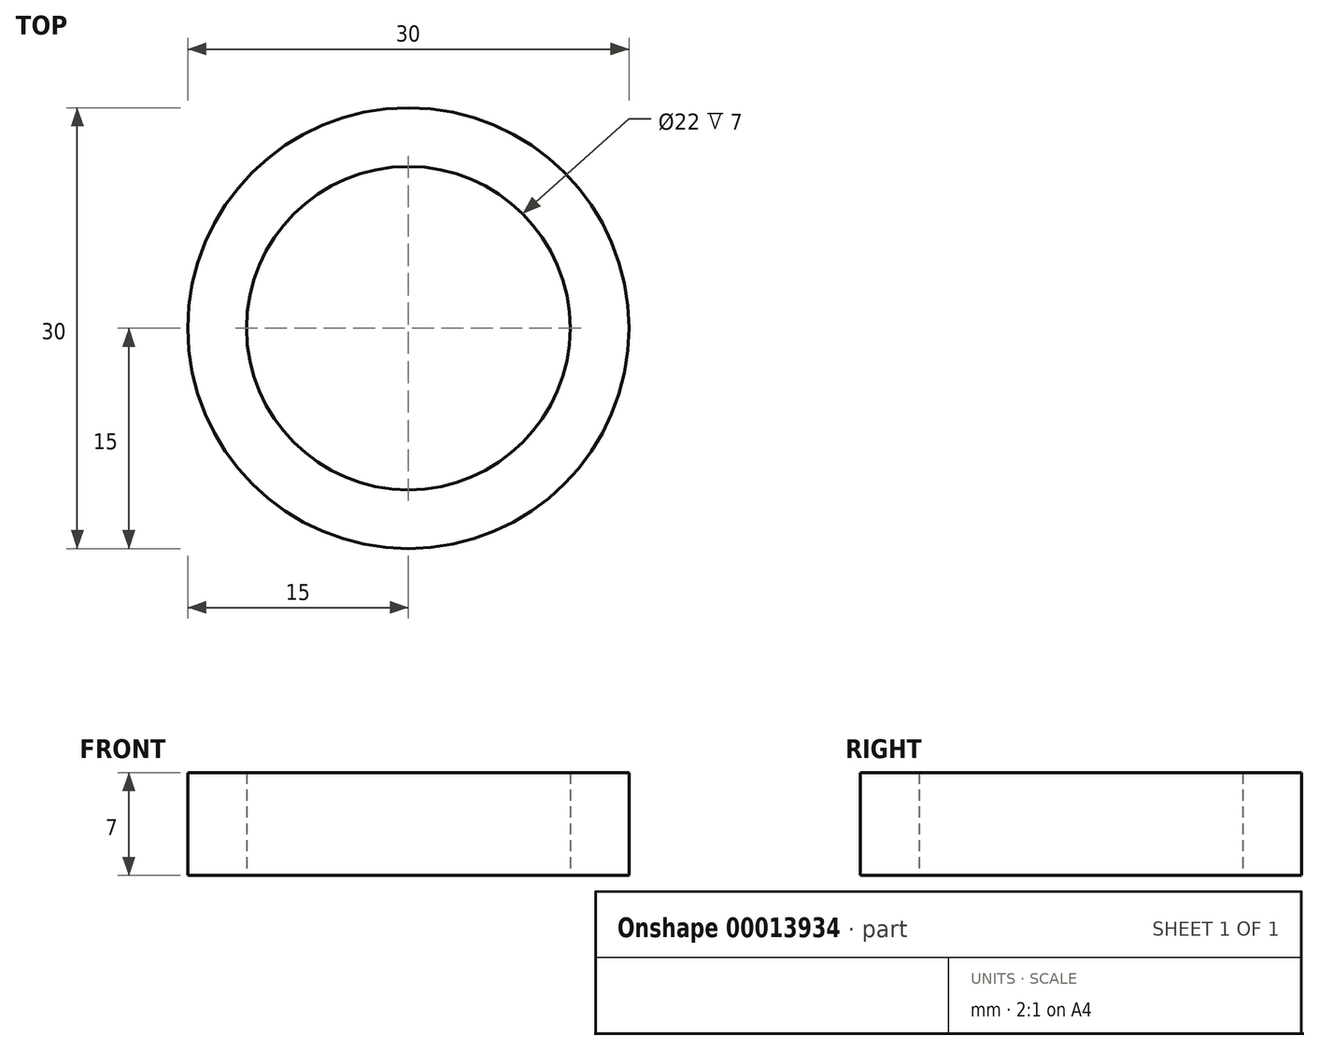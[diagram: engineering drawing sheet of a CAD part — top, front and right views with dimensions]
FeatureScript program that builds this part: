
annotation { "Feature Type Name" : "Feature", "Feature Type Description" : "" }
export const myFeature = defineFeature(function(context is Context, id is Id, definition is map)
    precondition{}
    {
        {
            var Q0;
            Q0=qCreatedBy(makeId("Top.planeOp"),FACE);
            var sketch = newSketch(context, id + "F0", { "sketchPlane" : qUnion([Q0])});
            skCircle(sketch, "E0", {"center": v(0, 0) * mm, "radius": 11 * mm});
            skCircle(sketch, "E1", {"center": v(0, 0) * mm, "radius": 15 * mm});
            skSolve(sketch);
        }
        {
            var Q0;
            Q0=makeQuery(id+"F0.imprint","IMPRINT",FACE,{"disambiguationData":[TD([[makeQuery(id+"F0.imprint","IMPRINT",EDGE,{"derivedFrom":sQuery(id+"F0.wireOp",EDGE,"E0")}),-1.0]])]});
            extrude(context, id + "F1", {"entities" : qUnion([Q0]), "depth" : 7 * mm});
        }
    });
